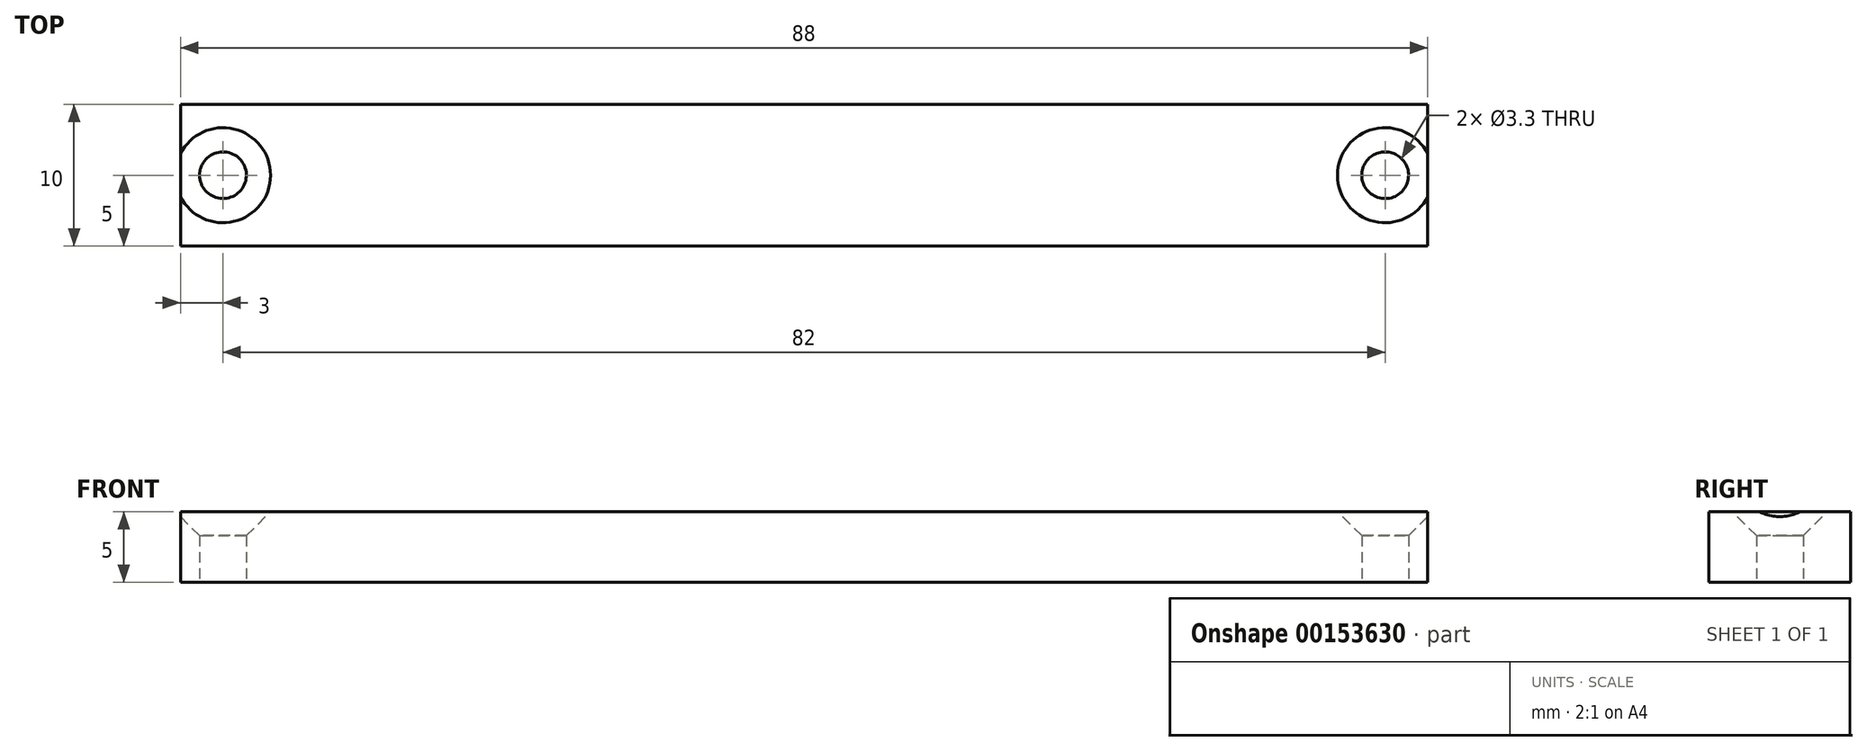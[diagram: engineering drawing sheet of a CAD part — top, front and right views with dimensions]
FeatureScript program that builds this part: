
annotation { "Feature Type Name" : "Feature", "Feature Type Description" : "" }
export const myFeature = defineFeature(function(context is Context, id is Id, definition is map)
    precondition{}
    {
        {
            var Q0;
            Q0=qCreatedBy(makeId("Top.planeOp"),FACE);
            var sketch = newSketch(context, id + "F0", { "sketchPlane" : qUnion([Q0])});
            skLineSegment(sketch, "E0.bottom", {"start": v(0, 0) * mm, "end": v(88, 0) * mm});
            skLineSegment(sketch, "E0.top", {"start": v(0, 10) * mm, "end": v(88, 10) * mm});
            skLineSegment(sketch, "E0.left", {"start": v(0, 0) * mm, "end": v(0, 10) * mm});
            skLineSegment(sketch, "E0.right", {"start": v(88, 0) * mm, "end": v(88, 10) * mm});
            skSolve(sketch);
        }
        {
            var Q0;
            Q0=makeQuery(id+"F0.imprint","IMPRINT",FACE,{"disambiguationData":[TD([[makeQuery(id+"F0.imprint","IMPRINT",EDGE,{"derivedFrom":sQuery(id+"F0.wireOp",EDGE,"E0.bottom")}),1.0]])]});
            extrude(context, id + "F1", {"entities" : qUnion([Q0]), "depth" : 5 * mm});
        }
        {
            var Q0;
            Q0=makeQuery(id+"F1.opExtrude","CAP_FACE",FACE,{"disambiguationData":[OSD([sQuery(id+"F0.wireOp",EDGE,"E0.bottom"),sQuery(id+"F0.wireOp",EDGE,"E0.top"),sQuery(id+"F0.wireOp",EDGE,"E0.left"),sQuery(id+"F0.wireOp",EDGE,"E0.right")])],"isStart":false});
            var sketch = newSketch(context, id + "F2", { "sketchPlane" : qUnion([Q0])});
            skCircle(sketch, "E1", {"center": v(3, 5) * mm, "radius": 1.87 * mm});
            skPoint(sketch, "E1.centerSnap0", {"position": v(0, 5) * mm});
            skCircle(sketch, "E2", {"center": v(85, 5) * mm, "radius": 2.65 * mm});
            skPoint(sketch, "E2.centerSnap0", {"position": v(88, 5) * mm});
            skSolve(sketch);
        }
        {
            var Q0;
            Q0=sQuery(id+"F2.wireOp",VERTEX,"E2.center");
            var Q1;
            Q1=sQuery(id+"F2.wireOp",VERTEX,"E1.center");
            var Q2;
            Q2=makeQuery(id+"F1.opExtrude","SWEPT_BODY",BODY,{"disambiguationData":[OSD([sQuery(id+"F0.wireOp",EDGE,"E0.bottom"),sQuery(id+"F0.wireOp",EDGE,"E0.top"),sQuery(id+"F0.wireOp",EDGE,"E0.left"),sQuery(id+"F0.wireOp",EDGE,"E0.right")])]});
            hole(context, id + "F3", {"style" : HoleStyle.C_SINK, "endStyle" : HoleEndStyle.BLIND, "standardTappedOrClearance" : lookupTablePath({ "standard" : "ISO", "fit" : "Normal", "size" : "M3", "type" : "Clearance" }), "standardBlindInLast" : lookupTablePath({ "fit" : "Standard", "standard" : "ISO", "size" : "M3", "type" : "Clearance" }), "holeDiameter" : 3.3 * mm, "cSinkDiameter" : 6.72 * mm, "cSinkAngle" : 90 * degree, "holeDepth" : 15 * mm, "locations" : qUnion([Q0, Q1]), "scope" : qUnion([Q2])});
        }
    });
